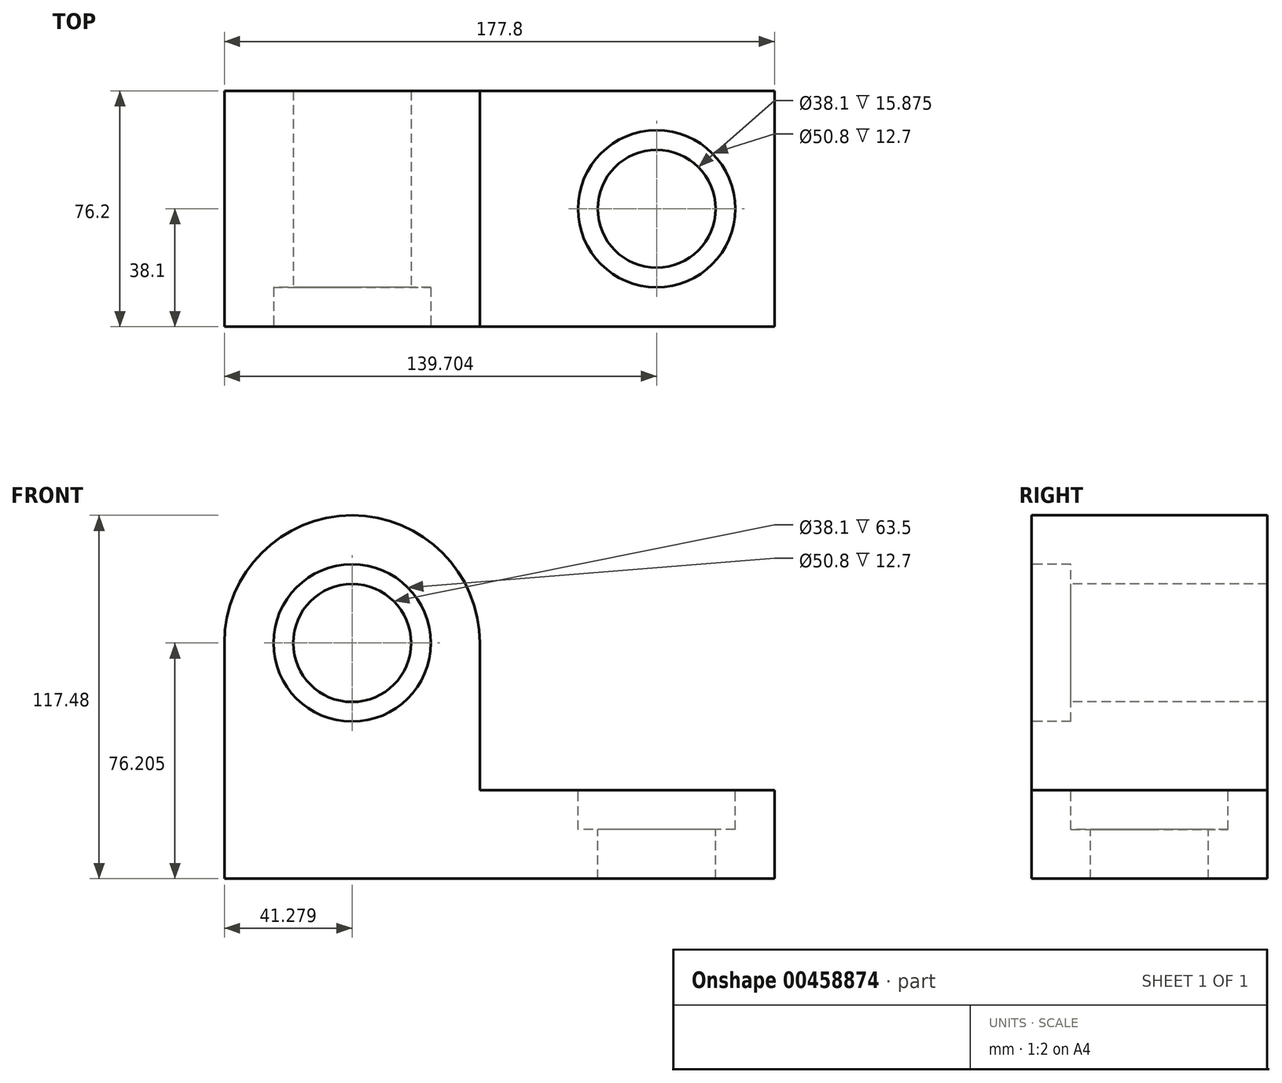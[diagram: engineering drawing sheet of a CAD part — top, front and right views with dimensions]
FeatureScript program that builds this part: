
annotation { "Feature Type Name" : "Feature", "Feature Type Description" : "" }
export const myFeature = defineFeature(function(context is Context, id is Id, definition is map)
    precondition{}
    {
        {
            var Q0;
            Q0=qCreatedBy(makeId("Front.planeOp"),FACE);
            var sketch = newSketch(context, id + "F0", { "sketchPlane" : qUnion([Q0])});
            skLineSegment(sketch, "E0", {"start": v(-58.06, -60.4) * mm, "end": v(119.74, -60.4) * mm});
            skLineSegment(sketch, "E1", {"start": v(119.74, -60.4) * mm, "end": v(119.74, -31.83) * mm});
            skArc(sketch, "E2", {"start": v(-58.06, 15.8) * mm, "mid": v(-45.97, 44.98) * mm, "end": v(-16.78, 57.07) * mm});
            skLineSegment(sketch, "E3", {"start": v(-16.78, 57.07) * mm, "end": v(-16.78, -60.4) * mm, "construction": true});
            skArc(sketch, "E4.MirrorCS", {"start": v(24.5, 15.8) * mm, "mid": v(12.4, 44.98) * mm, "end": v(-16.78, 57.07) * mm});
            skLineSegment(sketch, "E5", {"start": v(-58.06, 15.8) * mm, "end": v(-58.06, -60.4) * mm});
            skLineSegment(sketch, "E6", {"start": v(24.5, 15.8) * mm, "end": v(24.5, -31.83) * mm});
            skLineSegment(sketch, "E7", {"start": v(24.5, -31.83) * mm, "end": v(119.74, -31.83) * mm});
            skSolve(sketch);
        }
        {
            var Q0;
            Q0=makeQuery(id+"F0.imprint","IMPRINT",FACE,{"disambiguationData":[TD([[makeQuery(id+"F0.imprint","IMPRINT",EDGE,{"derivedFrom":sQuery(id+"F0.wireOp",EDGE,"E0")}),1.0]])]});
            extrude(context, id + "F1", {"entities" : qUnion([Q0]), "depth" : 76.2 * mm});
        }
        {
            var Q0;
            Q0=makeQuery(id+"F1.opExtrude","CAP_FACE",FACE,{"disambiguationData":[OSD([sQuery(id+"F0.wireOp",EDGE,"E0"),sQuery(id+"F0.wireOp",EDGE,"E1"),sQuery(id+"F0.wireOp",EDGE,"E2"),sQuery(id+"F0.wireOp",EDGE,"E4.MirrorCS"),sQuery(id+"F0.wireOp",EDGE,"E5"),sQuery(id+"F0.wireOp",EDGE,"E6"),sQuery(id+"F0.wireOp",EDGE,"E7")])],"isStart":false});
            var sketch = newSketch(context, id + "F2", { "sketchPlane" : qUnion([Q0])});
            skPoint(sketch, "E8", {"position": v(-16.78, 15.8) * mm});
            skSolve(sketch);
        }
        {
            var Q0;
            Q0=sQuery(id+"F2.wireOp",VERTEX,"E8");
            var Q1;
            Q1=makeQuery(id+"F1.opExtrude","SWEPT_BODY",BODY,{"disambiguationData":[OSD([sQuery(id+"F0.wireOp",EDGE,"E0"),sQuery(id+"F0.wireOp",EDGE,"E1"),sQuery(id+"F0.wireOp",EDGE,"E2"),sQuery(id+"F0.wireOp",EDGE,"E4.MirrorCS"),sQuery(id+"F0.wireOp",EDGE,"E5"),sQuery(id+"F0.wireOp",EDGE,"E6"),sQuery(id+"F0.wireOp",EDGE,"E7")])]});
            hole(context, id + "F3", {"style" : HoleStyle.C_BORE, "endStyle" : HoleEndStyle.THROUGH, "holeDiameter" : 38.1 * mm, "cBoreDiameter" : 50.8 * mm, "cBoreDepth" : 12.7 * mm, "isTappedThrough" : true, "tappedDepth" : 12.7 * mm, "tapClearance" : 3, "startFromSketch" : true, "locations" : qUnion([Q0]), "scope" : qUnion([Q1])});
        }
        {
            var Q0;
            Q0=makeQuery(id+"F1.opExtrude","SWEPT_FACE",FACE,{"disambiguationData":[OSD([sQuery(id+"F0.wireOp",EDGE,"E7")])]});
            var sketch = newSketch(context, id + "F4", { "sketchPlane" : qUnion([Q0])});
            skPoint(sketch, "E9", {"position": v(81.64, -38.1) * mm});
            skSolve(sketch);
        }
        {
            var Q0;
            Q0=sQuery(id+"F4.wireOp",VERTEX,"E9");
            var Q1;
            Q1=makeQuery(id+"F1.opExtrude","SWEPT_BODY",BODY,{"disambiguationData":[OSD([sQuery(id+"F0.wireOp",EDGE,"E0"),sQuery(id+"F0.wireOp",EDGE,"E1"),sQuery(id+"F0.wireOp",EDGE,"E2"),sQuery(id+"F0.wireOp",EDGE,"E4.MirrorCS"),sQuery(id+"F0.wireOp",EDGE,"E5"),sQuery(id+"F0.wireOp",EDGE,"E6"),sQuery(id+"F0.wireOp",EDGE,"E7")])]});
            hole(context, id + "F5", {"style" : HoleStyle.C_BORE, "endStyle" : HoleEndStyle.THROUGH, "holeDiameter" : 38.1 * mm, "cBoreDiameter" : 50.8 * mm, "cBoreDepth" : 12.7 * mm, "isTappedThrough" : true, "tappedDepth" : 12.7 * mm, "tapClearance" : 3, "startFromSketch" : true, "locations" : qUnion([Q0]), "scope" : qUnion([Q1])});
        }
    });
